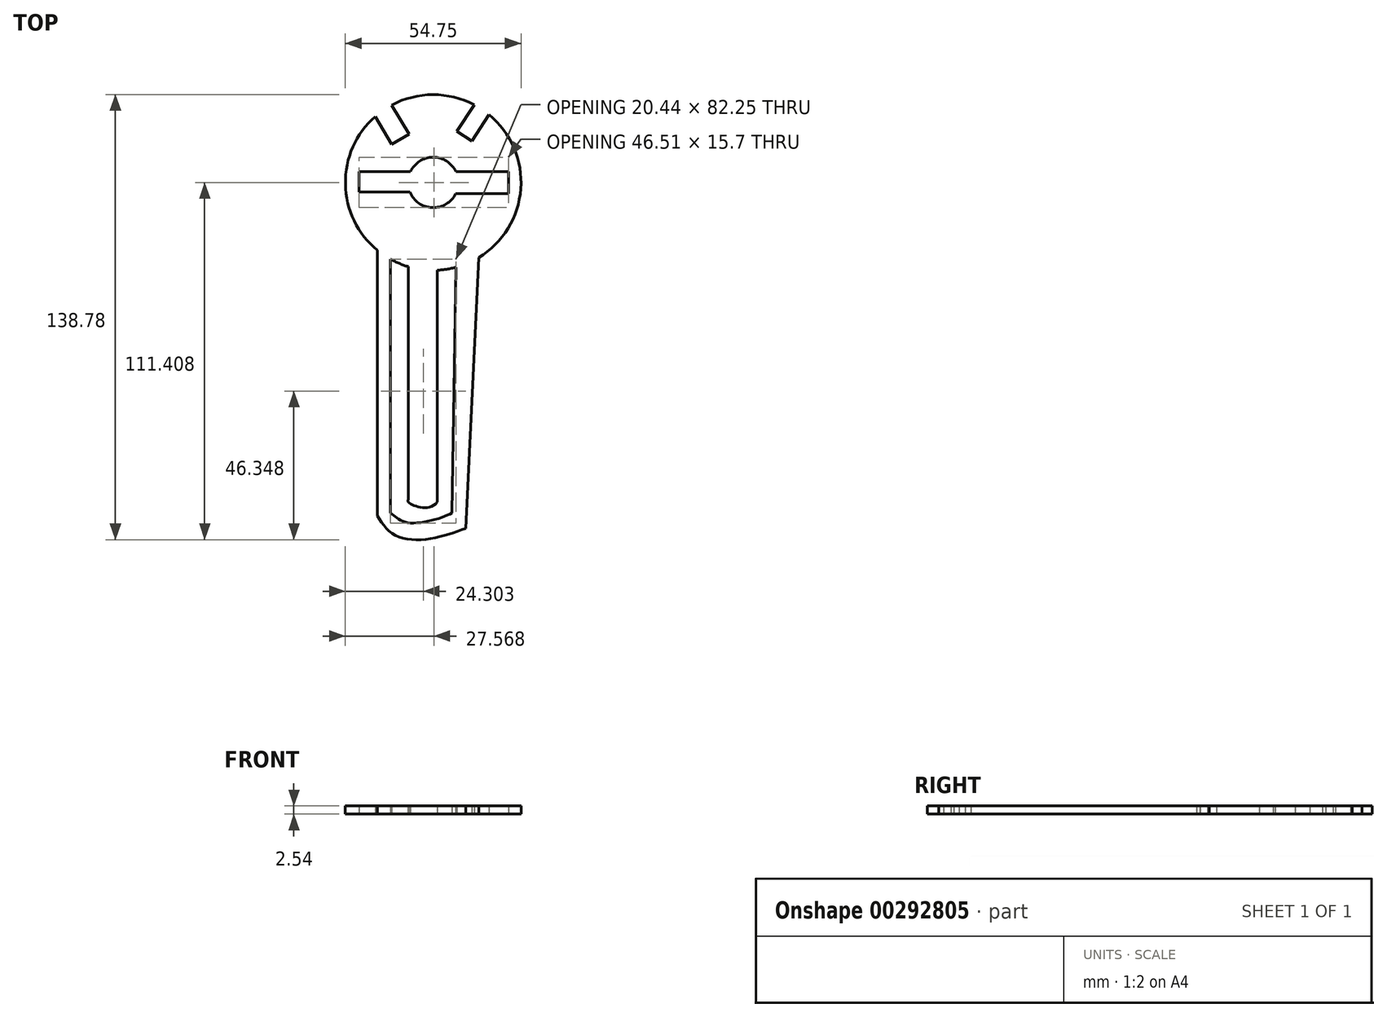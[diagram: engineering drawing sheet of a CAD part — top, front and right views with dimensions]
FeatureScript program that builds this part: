
annotation { "Feature Type Name" : "Feature", "Feature Type Description" : "" }
export const myFeature = defineFeature(function(context is Context, id is Id, definition is map)
    precondition{}
    {
        {
            var Q0;
            Q0=qCreatedBy(makeId("Top.planeOp"),FACE);
            var sketch = newSketch(context, id + "F0", { "sketchPlane" : qUnion([Q0])});
            skCircle(sketch, "E0", {"center": v(-27.25, 46.5) * mm, "radius": 27.37 * mm});
            skPoint(sketch, "E0.first.point", {"position": v(-45.33, 67.06) * mm});
            skPoint(sketch, "E0.second.point", {"position": v(-7.07, 28.01) * mm});
            skPoint(sketch, "E0.third.point", {"position": v(-44.62, 25.35) * mm});
            skLineSegment(sketch, "E1", {"start": v(-45.33, 67.06) * mm, "end": v(-40.18, 58.4) * mm});
            skLineSegment(sketch, "E2", {"start": v(-40.18, 58.4) * mm, "end": v(-34.8, 61.6) * mm});
            skLineSegment(sketch, "E3", {"start": v(-34.8, 61.6) * mm, "end": v(-40.18, 70.63) * mm});
            skLineSegment(sketch, "E4", {"start": v(-14.43, 70.7) * mm, "end": v(-19.84, 62.42) * mm});
            skLineSegment(sketch, "E5", {"start": v(-19.84, 62.42) * mm, "end": v(-15.19, 59.38) * mm});
            skLineSegment(sketch, "E6", {"start": v(-15.19, 59.38) * mm, "end": v(-9.8, 67.6) * mm});
            skFitSpline(sketch, "E7", {"points": [v(-44.62, 25.35) * mm, v(-44.62, -57.42) * mm], "startDerivative": vector(0, -81.78) * mm, "endDerivative": vector(0, -81.78) * mm});
            skFitSpline(sketch, "E8", {"points": [v(-44.62, -57.42) * mm, v(-39.28, -63.41) * mm, v(-28.5, -64.6) * mm, v(-17.12, -61.31) * mm], "startDerivative": vector(14.37, -23.17) * mm, "endDerivative": vector(28.03, 10.66) * mm});
            skLineSegment(sketch, "E9", {"start": v(-13.07, 23.09) * mm, "end": v(-17.12, -61.31) * mm});
            skLineSegment(sketch, "E10", {"start": v(-40.54, 22.57) * mm, "end": v(-40.54, -56.55) * mm});
            skFitSpline(sketch, "E11", {"points": [v(-40.54, -56.55) * mm, v(-35.02, -59.59) * mm, v(-21.42, -56.55) * mm], "startDerivative": vector(10.8, -7.08) * mm, "endDerivative": vector(12.73, 7.27) * mm});
            skLineSegment(sketch, "E12", {"start": v(-25.94, -53.1) * mm, "end": v(-25.94, 19.16) * mm});
            skLineSegment(sketch, "E13", {"start": v(-20.1, 20.08) * mm, "end": v(-21.42, -56.55) * mm});
            skLineSegment(sketch, "E14", {"start": v(-35.02, 20.26) * mm, "end": v(-35.02, -51.22) * mm});
            skFitSpline(sketch, "E15", {"points": [v(-35.02, -51.22) * mm, v(-35.02, -53.1) * mm, v(-25.94, -53.1) * mm], "startDerivative": vector(1.83, -12.47) * mm, "endDerivative": vector(12.42, 15.41) * mm});
            skPoint(sketch, "E16.2.internal.orphan", {"position": v(-33.54, -52.52) * mm});
            skCircle(sketch, "E17", {"center": v(-27.25, 46.5) * mm, "radius": 7.85 * mm});
            skPoint(sketch, "E18.end.orphan", {"position": v(0, 43.89) * mm});
            skLineSegment(sketch, "E19", {"start": v(-54.42, 49.83) * mm, "end": v(-34.36, 49.83) * mm});
            skLineSegment(sketch, "E20", {"start": v(-54.46, 43.55) * mm, "end": v(-34.52, 43.55) * mm});
            skLineSegment(sketch, "E21", {"start": v(-50.3, 49.83) * mm, "end": v(-50.3, 43.55) * mm});
            skLineSegment(sketch, "E22", {"start": v(-20.13, 49.83) * mm, "end": v(-0.08, 49.83) * mm});
            skLineSegment(sketch, "E23", {"start": v(-20.23, 43) * mm, "end": v(0, 43) * mm});
            skLineSegment(sketch, "E24", {"start": v(-3.8, 49.83) * mm, "end": v(-3.8, 43) * mm});
            skSolve(sketch);
        }
        {
            var Q0;
            {var subQ0=sQuery(id+"F0.wireOp",EDGE,"E7");Q0=makeQuery(id+"F0.imprint","IMPRINT",FACE,{"disambiguationData":[TD([[makeQuery(id+"F0.imprint","IMPRINT",EDGE,{"derivedFrom":subQ0}),1.0]])]});}
            var Q1;
            {var subQ5=sQuery(id+"F0.wireOp",EDGE,"E21");Q1=makeQuery(id+"F0.imprint","IMPRINT",FACE,{"disambiguationData":[TD([[makeQuery(id+"F0.imprint","IMPRINT",EDGE,{"derivedFrom":subQ5}),-1.0]])]});}
            var Q2;
            {var subQ5=sQuery(id+"F0.wireOp",EDGE,"E24");Q2=makeQuery(id+"F0.imprint","IMPRINT",FACE,{"disambiguationData":[TD([[makeQuery(id+"F0.imprint","IMPRINT",EDGE,{"derivedFrom":subQ5}),1.0]])]});}
            var Q3;
            {var subQ11=sQuery(id+"F0.wireOp",EDGE,"E1");Q3=makeQuery(id+"F0.imprint","IMPRINT",FACE,{"disambiguationData":[TD([[makeQuery(id+"F0.imprint","IMPRINT",EDGE,{"derivedFrom":subQ11}),-1.0]])]});}
            var Q4;
            {var subQ4=sQuery(id+"F0.wireOp",EDGE,"E0");var subQ11=makeQuery(id+"F0.imprint","INTERSECT",VERTEX,{"derivedFrom":[subQ4,sQuery(id+"F0.wireOp",EDGE,"E7")]});Q4=makeQuery(id+"F0.imprint","IMPRINT",FACE,{"disambiguationData":[TD([[makeQuery(id+"F0.imprint","IMPRINT",EDGE,{"disambiguationData":[TD([[subQ11,1.0]])],"derivedFrom":subQ4}),1.0]])]});}
            var Q5;
            {var subQ0=sQuery(id+"F0.wireOp",EDGE,"E12");Q5=makeQuery(id+"F0.imprint","IMPRINT",FACE,{"disambiguationData":[TD([[makeQuery(id+"F0.imprint","IMPRINT",EDGE,{"derivedFrom":subQ0}),1.0]])]});}
            extrude(context, id + "F1", {"entities" : qUnion([Q0, Q1, Q2, Q3, Q4, Q5]), "depth" : 2.54 * mm});
        }
    });
